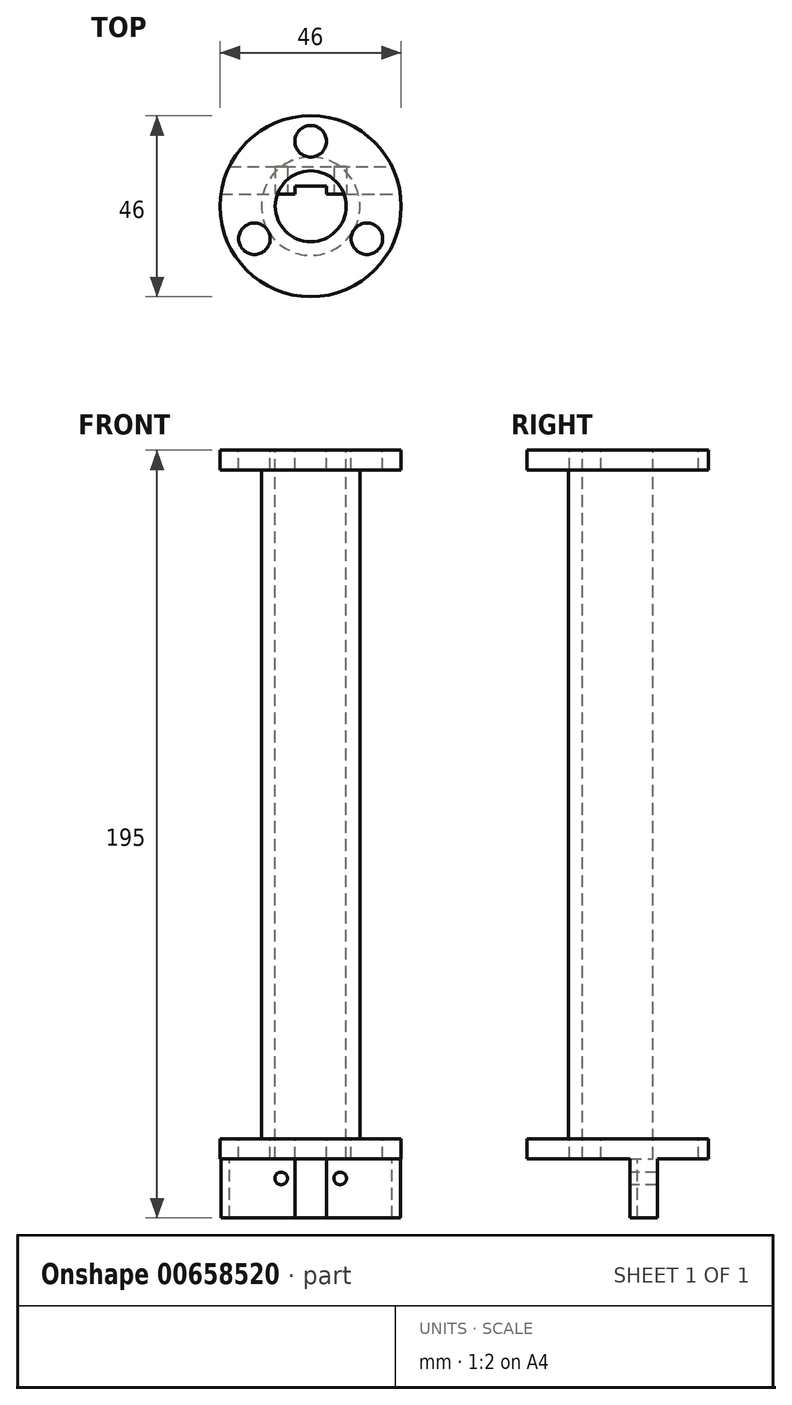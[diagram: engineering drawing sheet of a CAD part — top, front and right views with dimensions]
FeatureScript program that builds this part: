
annotation { "Feature Type Name" : "Feature", "Feature Type Description" : "" }
export const myFeature = defineFeature(function(context is Context, id is Id, definition is map)
    precondition{}
    {
        {
            var Q0;
            Q0=qCreatedBy(makeId("Front.planeOp"),FACE);
            var sketch = newSketch(context, id + "F0", { "sketchPlane" : qUnion([Q0])});
            skLineSegment(sketch, "E0.bottom", {"start": v(9, 85) * mm, "end": v(12.5, 85) * mm});
            skLineSegment(sketch, "E0.top", {"start": v(9, -85) * mm, "end": v(12.5, -85) * mm});
            skLineSegment(sketch, "E0.left", {"start": v(9, 85) * mm, "end": v(9, -85) * mm});
            skLineSegment(sketch, "E0.right", {"start": v(12.5, 85) * mm, "end": v(12.5, -85) * mm});
            skLineSegment(sketch, "E1.bottom", {"start": v(9, 85) * mm, "end": v(23, 85) * mm});
            skLineSegment(sketch, "E1.top", {"start": v(9, 90) * mm, "end": v(23, 90) * mm});
            skLineSegment(sketch, "E1.left", {"start": v(9, 85) * mm, "end": v(9, 90) * mm});
            skLineSegment(sketch, "E1.right", {"start": v(23, 85) * mm, "end": v(23, 90) * mm});
            skLineSegment(sketch, "E2.bottom", {"start": v(9, -85) * mm, "end": v(23, -85) * mm});
            skLineSegment(sketch, "E2.top", {"start": v(9, -90) * mm, "end": v(23, -90) * mm});
            skLineSegment(sketch, "E2.left", {"start": v(9, -85) * mm, "end": v(9, -90) * mm});
            skLineSegment(sketch, "E2.right", {"start": v(23, -85) * mm, "end": v(23, -90) * mm});
            skLineSegment(sketch, "E3", {"start": v(0, 90) * mm, "end": v(0, -90) * mm});
            skSolve(sketch);
        }
        {
            var Q0;
            {var subQ0=sQuery(id+"F0.wireOp",EDGE,"E0.left");Q0=makeQuery(id+"F0.imprint","IMPRINT",FACE,{"disambiguationData":[TD([[makeQuery(id+"F0.imprint","IMPRINT",EDGE,{"derivedFrom":subQ0}),1.0]])]});}
            var Q1;
            Q1=makeQuery(id+"F0.imprint","IMPRINT",FACE,{"disambiguationData":[TD([[makeQuery(id+"F0.imprint","IMPRINT",EDGE,{"derivedFrom":sQuery(id+"F0.wireOp",EDGE,"E1.top")}),-1.0]])]});
            var Q2;
            Q2=makeQuery(id+"F0.imprint","IMPRINT",FACE,{"disambiguationData":[TD([[makeQuery(id+"F0.imprint","IMPRINT",EDGE,{"derivedFrom":sQuery(id+"F0.wireOp",EDGE,"E2.top")}),1.0]])]});
            var Q3;
            Q3=sQuery(id+"F0.wireOp",EDGE,"E3");
            var Q4;
            Q4=sQuery(id+"F0.wireOp",EDGE,"E0.left");
            var Q5;
            Q5=sQuery(id+"F0.wireOp",EDGE,"E0.right");
            var Q6;
            Q6=sQuery(id+"F0.wireOp",EDGE,"E1.bottom");
            var Q7;
            Q7=sQuery(id+"F0.wireOp",EDGE,"E1.top");
            var Q8;
            Q8=sQuery(id+"F0.wireOp",EDGE,"E1.left");
            var Q9;
            Q9=sQuery(id+"F0.wireOp",EDGE,"E1.right");
            var Q10;
            Q10=sQuery(id+"F0.wireOp",EDGE,"E2.left");
            var Q11;
            Q11=sQuery(id+"F0.wireOp",EDGE,"E2.top");
            var Q12;
            Q12=sQuery(id+"F0.wireOp",EDGE,"E2.right");
            var Q13;
            Q13=sQuery(id+"F0.wireOp",EDGE,"E2.bottom");
            var Q14;
            Q14=sQuery(id+"F0.wireOp",EDGE,"E3");
            revolve(context, id + "F1", {"entities" : qUnion([Q0, Q1, Q2]), "surfaceEntities" : qUnion([Q3, Q4, Q5, Q6, Q7, Q8, Q9, Q10, Q11, Q12, Q13]), "axis" : qUnion([Q14]), "revolveType" : RevolveType.FULL});
        }
        {
            var Q0;
            Q0=makeQuery(id+"F1.opRevolve","SWEPT_FACE",FACE,{"disambiguationData":[OSD([sQuery(id+"F0.wireOp",EDGE,"E2.top")])]});
            var sketch = newSketch(context, id + "F2", { "sketchPlane" : qUnion([Q0])});
            skLineSegment(sketch, "E4.top", {"start": v(-20.66, -10.1) * mm, "end": v(20.66, -10.1) * mm});
            skLineSegment(sketch, "E5", {"start": v(-22.8, -3.08) * mm, "end": v(-4, -3.08) * mm});
            skLineSegment(sketch, "E6", {"start": v(-4, -3.08) * mm, "end": v(-4, -5.08) * mm});
            skLineSegment(sketch, "E7", {"start": v(-4, -5.08) * mm, "end": v(4, -5.08) * mm});
            skLineSegment(sketch, "E8", {"start": v(4, -5.08) * mm, "end": v(4, -3.08) * mm});
            skLineSegment(sketch, "E9", {"start": v(4, -3.08) * mm, "end": v(22.8, -3.08) * mm});
            skArc(sketch, "E10", {"start": v(20.66, -10.1) * mm, "mid": v(22, -6.68) * mm, "end": v(22.8, -3.08) * mm});
            skArc(sketch, "E11", {"start": v(-22.8, -3.08) * mm, "mid": v(-22, -6.68) * mm, "end": v(-20.66, -10.1) * mm});
            skSolve(sketch);
        }
        {
            var Q0;
            Q0 = qSketchRegion(id + "F2", true);
            extrude(context, id + "F3", {"entities" : qUnion([Q0]), "operationType" : NewBodyOperationType.ADD, "depth" : 15 * mm, "offsetDistance" : 25 * mm});
        }
        {
            var Q0;
            Q0=makeQuery(id+"F3.opExtrude","SWEPT_FACE",FACE,{"disambiguationData":[OSD([sQuery(id+"F2.wireOp",EDGE,"E5")])]});
            var sketch = newSketch(context, id + "F4", { "sketchPlane" : qUnion([Q0])});
            skPoint(sketch, "E12", {"position": v(-7.5, -95) * mm});
            skPoint(sketch, "E13", {"position": v(7.5, -95) * mm});
            skSolve(sketch);
        }
        {
            var Q0;
            Q0=sQuery(id+"F4.wireOp",VERTEX,"E12");
            var Q1;
            Q1=sQuery(id+"F4.wireOp",VERTEX,"E13");
            var Q2;
            Q2=makeQuery(id+"F1.opRevolve","SWEPT_BODY",BODY,{"disambiguationData":[OSD([sQuery(id+"F0.wireOp",EDGE,"E0.left"),sQuery(id+"F0.wireOp",EDGE,"E0.right"),sQuery(id+"F0.wireOp",EDGE,"E1.bottom"),sQuery(id+"F0.wireOp",EDGE,"E1.top"),sQuery(id+"F0.wireOp",EDGE,"E1.left"),sQuery(id+"F0.wireOp",EDGE,"E1.right"),sQuery(id+"F0.wireOp",EDGE,"E2.bottom"),sQuery(id+"F0.wireOp",EDGE,"E2.top"),sQuery(id+"F0.wireOp",EDGE,"E2.left"),sQuery(id+"F0.wireOp",EDGE,"E2.right")])]});
            hole(context, id + "F5", {"style" : HoleStyle.SIMPLE, "endStyle" : HoleEndStyle.THROUGH, "holeDiameter" : 3.2 * mm, "majorDiameter" : 5 * mm, "isTappedThrough" : true, "tappedDepth" : 12 * mm, "tapClearance" : 3, "locations" : qUnion([Q0, Q1]), "scope" : qUnion([Q2])});
        }
        {
            var Q0;
            Q0=makeQuery(id+"F1.opRevolve","SWEPT_FACE",FACE,{"disambiguationData":[OSD([sQuery(id+"F0.wireOp",EDGE,"E1.top")])]});
            var sketch = newSketch(context, id + "F6", { "sketchPlane" : qUnion([Q0])});
            skPoint(sketch, "E14", {"position": v(0, 16.5) * mm});
            skPoint(sketch, "E15.1.0", {"position": v(-14.29, -8.25) * mm});
            skPoint(sketch, "E15.2.0", {"position": v(14.29, -8.25) * mm});
            skPoint(sketch, "E15.center", {"position": v(0, 0) * mm});
            skSolve(sketch);
        }
        {
            var Q0;
            Q0=sQuery(id+"F6.wireOp",VERTEX,"E15.1.0");
            var Q1;
            Q1=sQuery(id+"F6.wireOp",VERTEX,"E14");
            var Q2;
            Q2=sQuery(id+"F6.wireOp",VERTEX,"E15.2.0");
            var Q3;
            Q3=makeQuery(id+"F1.opRevolve","SWEPT_BODY",BODY,{"disambiguationData":[OSD([sQuery(id+"F0.wireOp",EDGE,"E0.left"),sQuery(id+"F0.wireOp",EDGE,"E0.right"),sQuery(id+"F0.wireOp",EDGE,"E1.bottom"),sQuery(id+"F0.wireOp",EDGE,"E1.top"),sQuery(id+"F0.wireOp",EDGE,"E1.left"),sQuery(id+"F0.wireOp",EDGE,"E1.right"),sQuery(id+"F0.wireOp",EDGE,"E2.bottom"),sQuery(id+"F0.wireOp",EDGE,"E2.top"),sQuery(id+"F0.wireOp",EDGE,"E2.left"),sQuery(id+"F0.wireOp",EDGE,"E2.right")])]});
            hole(context, id + "F7", {"style" : HoleStyle.SIMPLE, "endStyle" : HoleEndStyle.THROUGH, "holeDiameter" : 8 * mm, "majorDiameter" : 5 * mm, "isTappedThrough" : true, "tappedDepth" : 12 * mm, "tapClearance" : 3, "locations" : qUnion([Q0, Q1, Q2]), "scope" : qUnion([Q3])});
        }
    });
